# Revit family: Haworth_Planes_CredenzaBase_AP_PRELIMINARY
name_source: partatom
category: Furniture Systems
units: mm (PartAtom-declared; Revit-internal decimal feet)

## family parameters
Always vertical = Yes
Cut with Voids When Loaded = No
OmniClass Number = 23.40.70.14.64.21
OmniClass Title = Systems Furniture
Part Type = Normal
Room Calculation Point = No
Round Connector Dimension = Use Diameter
Shared = No
Work Plane-Based = No

## types (8) — shared parameters
Actual Depth = 508 mm
Assembly Code = E2020200
Base Only = Yes
Custom Size = Yes
Description = Haworth - Planes - Credenza Base
Manufacturer = Haworth
Max. Height = 737 mm  [stored 2.41798 ft]
Max. Width = 2743 mm  [stored 8.99934 ft]
Min. Height = 483 mm
Min. Width = 914 mm  [stored 2.99869 ft]
Model = WOPLRBN
Revision Number = 1
Size = Verify Final Dim. w/ Haworth
URL = https://www.haworth.com
URL - Product = https://www.haworth.com
Warranty = http://www.haworth.com

## per-type parameters (varying)
| type | Actual Height | Actual Width | Double | Height | Width | Width Double | Width Single |
| 914w x 483h | 483 mm | 914 mm  [stored 2.99869 ft] | No | 483 mm | 914 mm  [stored 2.99869 ft] | 457 mm  [stored 1.49934 ft] | 914 mm  [stored 2.99869 ft] |
| 1372w x 483h | 483 mm | 1372 mm  [stored 4.50131 ft] | No | 483 mm | 1372 mm  [stored 4.50131 ft] | 686 mm  [stored 2.25066 ft] | 1372 mm  [stored 4.50131 ft] |
| 1829w x 483h | 483 mm | 1829 mm  [stored 6.00066 ft] | Yes | 483 mm | 1829 mm  [stored 6.00066 ft] | 915 mm | 915 mm |
| 2743w x 483h | 483 mm | 2743 mm  [stored 8.99934 ft] | Yes | 483 mm | 2743 mm  [stored 8.99934 ft] | 1372 mm  [stored 4.50131 ft] | 1372 mm  [stored 4.50131 ft] |
| 1372w x 737h | 737 mm  [stored 2.41798 ft] | 1372 mm  [stored 4.50131 ft] | No | 737 mm  [stored 2.41798 ft] | 1372 mm  [stored 4.50131 ft] | 686 mm  [stored 2.25066 ft] | 1372 mm  [stored 4.50131 ft] |
| 1829w x 737h | 737 mm  [stored 2.41798 ft] | 1829 mm  [stored 6.00066 ft] | Yes | 737 mm  [stored 2.41798 ft] | 1829 mm  [stored 6.00066 ft] | 915 mm | 915 mm |
| 2743w x 737h | 737 mm  [stored 2.41798 ft] | 2743 mm  [stored 8.99934 ft] | Yes | 737 mm  [stored 2.41798 ft] | 2743 mm  [stored 8.99934 ft] | 1372 mm  [stored 4.50131 ft] | 1372 mm  [stored 4.50131 ft] |
| 914w x 737h | 737 mm  [stored 2.41798 ft] | 914 mm  [stored 2.99869 ft] | No | 737 mm  [stored 2.41798 ft] | 914 mm  [stored 2.99869 ft] | 457 mm  [stored 1.49934 ft] | 914 mm  [stored 2.99869 ft] |

note: [stored X ft] marks values corroborated as IEEE doubles in the binary element streams (Revit-internal decimal feet)

## geometry (parser evidence)
native form markers: Sweep x24
no freeform markers — native parametric forms only
